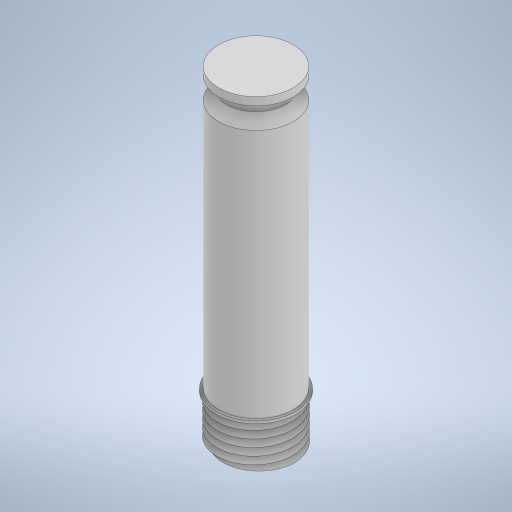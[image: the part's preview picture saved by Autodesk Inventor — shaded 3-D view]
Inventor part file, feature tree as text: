
AUTODESK INVENTOR PART (.ipt)
format: ipt  version: 2024 (Build 280153000, 153)  size: 390,144 bytes
history: native  units: mm
features: sketch x8, extrude x6, other x1, pattern_circular x1, revolve x1
ambient origin geometry x8: Origin, YZ Plane, XZ Plane, XY Plane, X Axis, Y Axis, Z Axis, Center Point
bodies: Volumenkörper1 (feature_tree)
feature tree (17):
  extrude  "Extrusion1"  Depth=61.0mm TaperAngle=0.0deg
  other  "Spirale1"
  extrude  "Extrusion9"  Depth=0.5mm
  extrude  "Extrusion6"  Depth=21.85mm
  pattern_circular  "Runde Anordnung1"  Count=4  [1 undecoded]
  extrude  "Extrusion10"  Depth=15.0mm
  extrude  "Extrusion11"  Depth=10.0mm
  revolve  "Umdrehung1"
  extrude  "Extrusion12"  Depth=7.5mm
  sketch  "Skizze1"  dims[d0=15.0mm d1=61.0mm d2=0.0mm]
  sketch  "Skizze6"  dims[d24=360.0deg d32=0.5mm]
  sketch  "Skizze8"  dims[d33=0.6mm d34=0.6mm d35=40.0mm d36=21.85mm d37=0.0mm d38=0.0mm]
  sketch  "Skizze12"  dims[d39=60.0mm d40=360.0deg d54=15.0mm]
  sketch  "Skizze14"  dims[d58=1.4mm d59=9.85mm d60=10.0mm d61=0.0mm d62=90.0deg d63=90.0deg d64=0.0mm d65=0.0mm d68=15.0mm]
  sketch  "Skizze15"  dims[d69=52.8mm d70=0.0mm d73=7.5mm]
  sketch  "Skizze17"  dims[d75=14.5mm]
  sketch  "Skizze20"  dims[d76=15.0mm d77=27.0mm d78=21.85mm d79=0.0mm d80=0.0mm d86=60.0mm d87=0.0mm d89=1.5mm d90=4.0mm d91=1.5mm d92=1.4mm d93=60.0deg d94=0.4mm d95=8.2mm d96=0.0mm d52=0.0mm d53=0.0mm d55=0.0mm]
note: 1 required parameter value undecoded (feature->parameter linkage not recoverable at this tier; creation-order binding heuristic only, values carry confidence <= 0.55)
